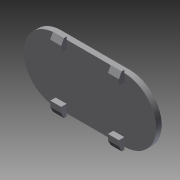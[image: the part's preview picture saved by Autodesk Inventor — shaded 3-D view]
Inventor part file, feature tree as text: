
AUTODESK INVENTOR PART (.ipt)
format: ipt  version: 2013 (Build 170138000, 138)  size: 108,544 bytes
history: native  units: in
note: dims shown in document units (in); Inventor stores cm internally (conversion verified against a paired STEP export)
features: chamfer x4, extrude x2, sketch x2
ambient origin geometry x8: Origin, YZ Plane, XZ Plane, XY Plane, X Axis, Y Axis, Z Axis, Center Point
bodies: Solid1 (feature_tree)
feature tree (8):
  extrude  "Extrusion1"  Depth=0.039in TaperAngle=0.0deg
  extrude  "Extrusion2"  Depth=0.02in TaperAngle=45.0deg
  chamfer  "Chamfer1"  Distance=0.02in Angle=45.0deg
  chamfer  "Chamfer2"  Distance=0.02in Angle=45.0deg
  chamfer  "Chamfer3"  [1 undecoded]
  chamfer  "Chamfer4"  [1 undecoded]
  sketch  "Sketch1"  dims[d0=0.039in d1=0.0in d2=0.039in d3=0.0in]
  sketch  "Sketch2"  dims[d4=0.02in d5=0.039in d6=45.0deg d7=0.02in d8=0.039in d9=45.0deg d10=0.02in d11=0.039in d12=45.0deg d13=0.02in d14=0.039in d15=45.0deg]
note: 2 required parameter values undecoded (feature->parameter linkage not recoverable at this tier; creation-order binding heuristic only, values carry confidence <= 0.55)
